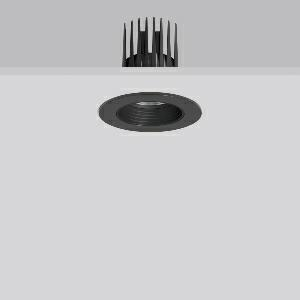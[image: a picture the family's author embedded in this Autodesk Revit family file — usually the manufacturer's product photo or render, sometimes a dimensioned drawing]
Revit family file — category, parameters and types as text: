
# Revit family: heledon_mini_e_901752_003_2_8350
name_source: partatom
category: Lighting Fixtures
units: mm (PartAtom-declared; Revit-internal decimal feet)

## family parameters
Cut with Voids When Loaded = No
Host = Face
Light Source = No
Part Type = Normal
Room Calculation Point = No
Round Connector Dimension = Use Diameter
Shared = No

## types (1)
- HELEDON mini E (1 x LED Modul 927, 2850 lm, 2700)
    Apparent Load = 29 VA
    Approval mark = CE
    CIE Flux Codes = 96 100 100 100 100
    Color Rendering = 92
    Color Temperature = 2700
    Default Elevation = 1800 mm
    Description = Series: HELEDON mini
Round recessed downlight. Housing: die-cast aluminium, powder-coated. Black plastic ring and recessed LED to prevent glare from the side. Optical assembly with lens made of plastic (polycarbonate) for the best homogeneous light distribution - can be changed without tools. Best colour rendering index Ra>90. Suitable for Recessed ceiling mounting. Installation without tools thanks to spring fastening system. Including separate LED converter with connecting cable 600 mm.High quality converter without flickering and stroboscopic effect. Through-wiring box (5 pole) available as accessory. The following accessories can be mounted without use of tools: interchangeable lenses, decorative glasses, honeycomb louvre, clear and frosted diffusers, white interchangeable plastic ring. 
Colour: deep black, matt (RAL 9005)
Diameter: 124 mm
Height: 3 mm
Cut-out diameter: 114 mm
Recess height: 170 mm
Luminaire: recess height: 120 mm
Lamp: LED
Socket: without socket
Colour temperature: 2700K
Colour rendering index (CRI): 92
System power: 29 W
Rated luminous flux: 2850 lm
Luminous efficiency: 98 lm/W
Control gear: Regulated power supply
Protection class: II
Type of protection: IP 20
    Height = 0 mm  [stored 0 ft]
    Lamp = 1 x LED Modul 927
    Lamp Light Flux = 2850 lm
    Lamp count = 1
    Length = 124 mm  [stored 0.406824 ft]
    Lifetime = 50000 h
    Luminous efficacy = 98 lm/W
    Manufacturer = RZB
    ModVariant = No
    Model = 901752.003.2
    Mounting Place = Ceiling
    Mounting Type = Recessed
    Number of Poles = 1
    OnlyDefault = Yes
    Power Factor = 1
    Product Name = HELEDON mini E
    Product group = Recessed downlights
    ProductGroupID = 402
    Protection Class = Protection class II
    Protection Degree = IP 20
    RLX_Detail_Level = 1
    RLX_Emergency_Light_Flux = 0 lm
    RLX_Emergency_Type = 0
    RLX_Emergency_Type_DB = No
    RlxData = <blob elided: 127689 chars, md5=74a3dda0>
    Socket = socket
    Standby Power = 0 W
    System Light Flux = 2850 lm
    System Power = 29 W
    Type Comments = Product without accessories
    Type Image = 901656.003.jpg
    URL = http://relux.com
    VarID = ---
    Voltage = 230 V
    Voltage Range = 220-240 V
    Weight = 0.00 kg
    Width = 0 mm  [stored 0 ft]

note: [stored X ft] marks values corroborated as IEEE doubles in the binary element streams (Revit-internal decimal feet)

## geometry (parser evidence)
native form markers: Blend x4, Sweep x13
no freeform markers — native parametric forms only
